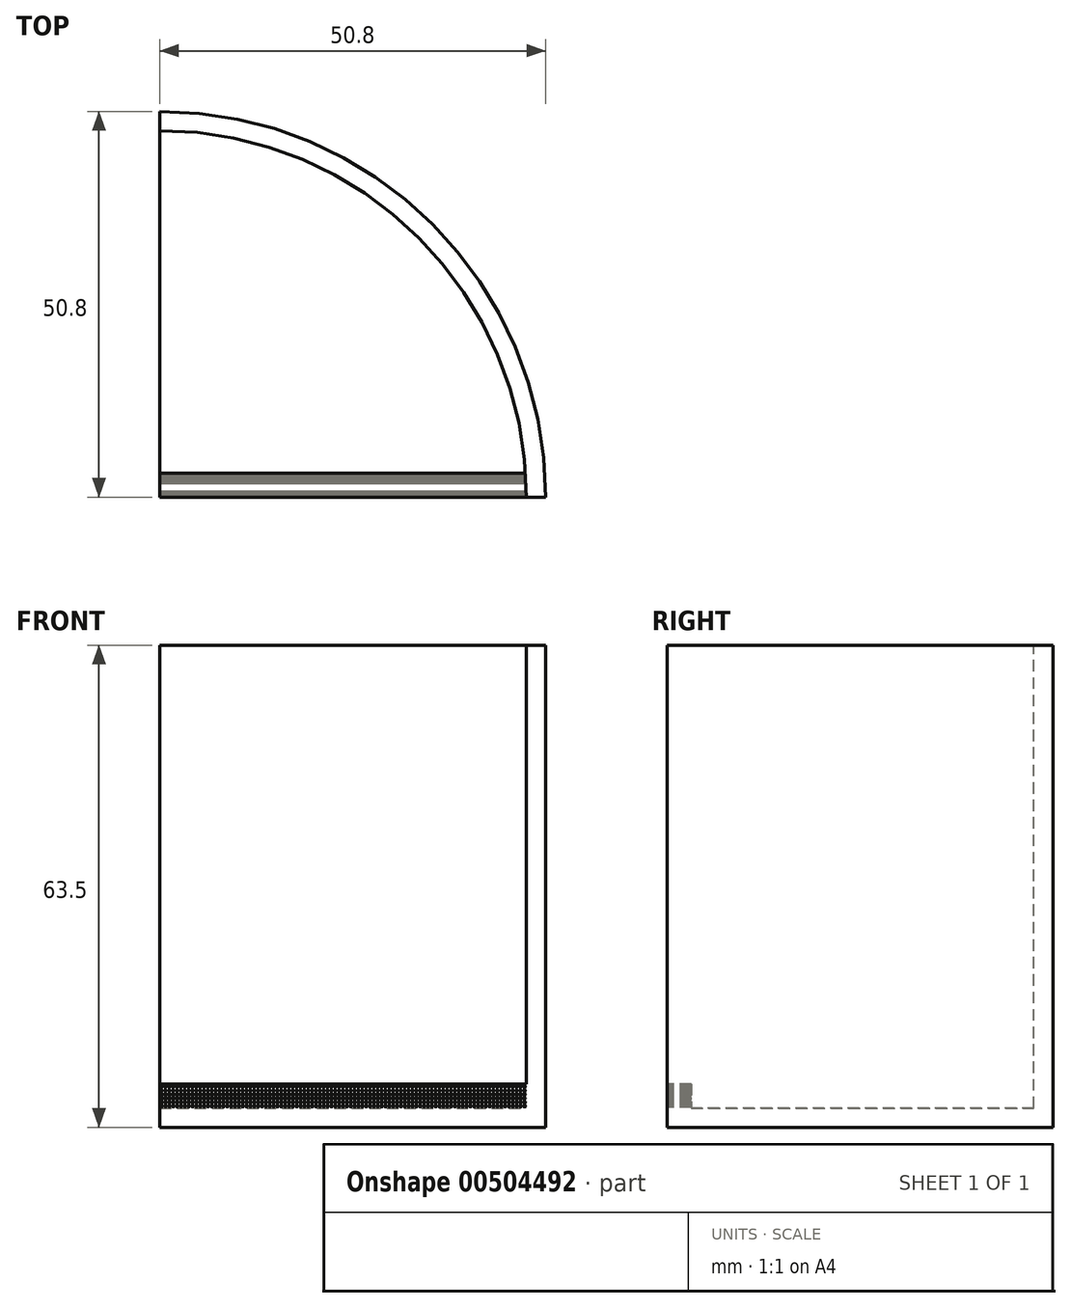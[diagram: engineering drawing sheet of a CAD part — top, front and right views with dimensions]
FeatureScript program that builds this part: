
annotation { "Feature Type Name" : "Feature", "Feature Type Description" : "" }
export const myFeature = defineFeature(function(context is Context, id is Id, definition is map)
    precondition{}
    {
        {
            var Q0;
            Q0=qCreatedBy(makeId("Front.planeOp"),FACE);
            var sketch = newSketch(context, id + "F0", { "sketchPlane" : qUnion([Q0])});
            skLineSegment(sketch, "E0", {"start": v(0, -22.85) * mm, "end": v(50.8, -22.85) * mm});
            skLineSegment(sketch, "E1", {"start": v(50.8, -22.85) * mm, "end": v(50.8, 40.65) * mm});
            skLineSegment(sketch, "E2", {"start": v(50.8, 40.65) * mm, "end": v(50.8, 40.65) * mm});
            skLineSegment(sketch, "E3", {"start": v(0, -22.85) * mm, "end": v(0, -20.3) * mm});
            skLineSegment(sketch, "E4", {"start": v(0, -20.3) * mm, "end": v(48.26, -20.3) * mm});
            skLineSegment(sketch, "E5", {"start": v(48.26, -20.3) * mm, "end": v(48.26, 40.65) * mm});
            skLineSegment(sketch, "E6", {"start": v(48.26, 40.65) * mm, "end": v(50.8, 40.65) * mm});
            skSolve(sketch);
        }
        {
            var Q0;
            Q0=makeQuery(id+"F0.imprint","IMPRINT",FACE,{"disambiguationData":[TD([[makeQuery(id+"F0.imprint","IMPRINT",EDGE,{"derivedFrom":sQuery(id+"F0.wireOp",EDGE,"E0")}),1.0]])]});
            var Q1;
            Q1=sQuery(id+"F0.wireOp",EDGE,"E3");
            revolve(context, id + "F1", {"entities" : qUnion([Q0]), "axis" : qUnion([Q1]), "revolveType" : RevolveType.ONE_DIRECTION, "angle" : 90 * degree});
        }
        {
            var Q0;
            Q0=makeQuery(id+"F1.opRevolve","CAP_FACE",FACE,{"disambiguationData":[OSD([sQuery(id+"F0.wireOp",EDGE,"E0"),sQuery(id+"F0.wireOp",EDGE,"E1"),sQuery(id+"F0.wireOp",EDGE,"E3"),sQuery(id+"F0.wireOp",EDGE,"E4"),sQuery(id+"F0.wireOp",EDGE,"E5"),sQuery(id+"F0.wireOp",EDGE,"E6")])],"isStart":true});
            var sketch = newSketch(context, id + "F2", { "sketchPlane" : qUnion([Q0])});
            skLineSegment(sketch, "E7.bottom", {"start": v(0, -20.3) * mm, "end": v(48.26, -20.3) * mm});
            skLineSegment(sketch, "E7.top", {"start": v(0, -17.13) * mm, "end": v(48.26, -17.13) * mm});
            skLineSegment(sketch, "E7.left", {"start": v(0, -20.3) * mm, "end": v(0, -17.13) * mm});
            skLineSegment(sketch, "E7.right", {"start": v(48.26, -20.3) * mm, "end": v(48.26, -17.13) * mm});
            skCircle(sketch, "E8", {"center": v(0.25, -20.05) * mm, "radius": 0.13 * mm});
            skLineSegment(sketch, "E9", {"start": v(0.25, -20.05) * mm, "end": v(0, -20.05) * mm});
            skCircle(sketch, "E10", {"center": v(0.25, -19.54) * mm, "radius": 0.13 * mm});
            skCircle(sketch, "E11", {"center": v(0.24, -19.04) * mm, "radius": 0.13 * mm});
            skCircle(sketch, "E12", {"center": v(0.24, -18.53) * mm, "radius": 0.13 * mm});
            skCircle(sketch, "E13", {"center": v(0.23, -18.02) * mm, "radius": 0.13 * mm});
            skCircle(sketch, "E14", {"center": v(0.23, -17.51) * mm, "radius": 0.13 * mm});
            skCircle(sketch, "E15.1.0.0", {"center": v(0.76, -20.05) * mm, "radius": 0.13 * mm});
            skCircle(sketch, "E15.2.0.0", {"center": v(1.27, -20.05) * mm, "radius": 0.13 * mm});
            skCircle(sketch, "E15.3.0.0", {"center": v(1.78, -20.05) * mm, "radius": 0.13 * mm});
            skCircle(sketch, "E15.4.0.0", {"center": v(2.29, -20.05) * mm, "radius": 0.13 * mm});
            skCircle(sketch, "E15.5.0.0", {"center": v(2.8, -20.05) * mm, "radius": 0.13 * mm});
            skCircle(sketch, "E15.6.0.0", {"center": v(3.3, -20.05) * mm, "radius": 0.13 * mm});
            skCircle(sketch, "E15.7.0.0", {"center": v(3.81, -20.05) * mm, "radius": 0.13 * mm});
            skCircle(sketch, "E15.8.0.0", {"center": v(4.32, -20.05) * mm, "radius": 0.13 * mm});
            skCircle(sketch, "E15.9.0.0", {"center": v(4.83, -20.05) * mm, "radius": 0.13 * mm});
            skCircle(sketch, "E15.10.0.0", {"center": v(5.33, -20.05) * mm, "radius": 0.13 * mm});
            skCircle(sketch, "E15.11.0.0", {"center": v(5.84, -20.05) * mm, "radius": 0.13 * mm});
            skCircle(sketch, "E15.12.0.0", {"center": v(6.35, -20.05) * mm, "radius": 0.13 * mm});
            skCircle(sketch, "E15.13.0.0", {"center": v(6.86, -20.05) * mm, "radius": 0.13 * mm});
            skCircle(sketch, "E15.14.0.0", {"center": v(7.37, -20.05) * mm, "radius": 0.13 * mm});
            skCircle(sketch, "E15.15.0.0", {"center": v(7.87, -20.05) * mm, "radius": 0.13 * mm});
            skCircle(sketch, "E15.16.0.0", {"center": v(8.38, -20.05) * mm, "radius": 0.13 * mm});
            skCircle(sketch, "E15.17.0.0", {"center": v(8.9, -20.05) * mm, "radius": 0.13 * mm});
            skCircle(sketch, "E15.18.0.0", {"center": v(9.4, -20.05) * mm, "radius": 0.13 * mm});
            skCircle(sketch, "E15.19.0.0", {"center": v(9.9, -20.05) * mm, "radius": 0.13 * mm});
            skCircle(sketch, "E15.20.0.0", {"center": v(10.41, -20.05) * mm, "radius": 0.13 * mm});
            skCircle(sketch, "E15.21.0.0", {"center": v(10.92, -20.05) * mm, "radius": 0.13 * mm});
            skCircle(sketch, "E15.22.0.0", {"center": v(11.43, -20.05) * mm, "radius": 0.13 * mm});
            skCircle(sketch, "E15.23.0.0", {"center": v(11.94, -20.05) * mm, "radius": 0.13 * mm});
            skCircle(sketch, "E15.24.0.0", {"center": v(12.45, -20.05) * mm, "radius": 0.13 * mm});
            skCircle(sketch, "E15.25.0.0", {"center": v(12.95, -20.05) * mm, "radius": 0.13 * mm});
            skCircle(sketch, "E15.26.0.0", {"center": v(13.46, -20.05) * mm, "radius": 0.13 * mm});
            skCircle(sketch, "E15.27.0.0", {"center": v(13.97, -20.05) * mm, "radius": 0.13 * mm});
            skCircle(sketch, "E15.28.0.0", {"center": v(14.48, -20.05) * mm, "radius": 0.13 * mm});
            skCircle(sketch, "E15.29.0.0", {"center": v(14.99, -20.05) * mm, "radius": 0.13 * mm});
            skCircle(sketch, "E15.30.0.0", {"center": v(15.5, -20.05) * mm, "radius": 0.13 * mm});
            skCircle(sketch, "E15.31.0.0", {"center": v(16, -20.05) * mm, "radius": 0.13 * mm});
            skCircle(sketch, "E15.32.0.0", {"center": v(16.51, -20.05) * mm, "radius": 0.13 * mm});
            skCircle(sketch, "E15.33.0.0", {"center": v(17.02, -20.05) * mm, "radius": 0.13 * mm});
            skCircle(sketch, "E15.34.0.0", {"center": v(17.53, -20.05) * mm, "radius": 0.13 * mm});
            skCircle(sketch, "E15.35.0.0", {"center": v(18.03, -20.05) * mm, "radius": 0.13 * mm});
            skCircle(sketch, "E15.36.0.0", {"center": v(18.54, -20.05) * mm, "radius": 0.13 * mm});
            skCircle(sketch, "E15.37.0.0", {"center": v(19.05, -20.05) * mm, "radius": 0.13 * mm});
            skCircle(sketch, "E15.38.0.0", {"center": v(19.56, -20.05) * mm, "radius": 0.13 * mm});
            skCircle(sketch, "E15.39.0.0", {"center": v(20.07, -20.05) * mm, "radius": 0.13 * mm});
            skCircle(sketch, "E15.40.0.0", {"center": v(20.57, -20.05) * mm, "radius": 0.13 * mm});
            skCircle(sketch, "E15.41.0.0", {"center": v(21.08, -20.05) * mm, "radius": 0.13 * mm});
            skCircle(sketch, "E15.42.0.0", {"center": v(21.6, -20.05) * mm, "radius": 0.13 * mm});
            skCircle(sketch, "E15.43.0.0", {"center": v(22.1, -20.05) * mm, "radius": 0.13 * mm});
            skCircle(sketch, "E15.44.0.0", {"center": v(22.6, -20.05) * mm, "radius": 0.13 * mm});
            skCircle(sketch, "E15.45.0.0", {"center": v(23.11, -20.05) * mm, "radius": 0.13 * mm});
            skCircle(sketch, "E15.46.0.0", {"center": v(23.62, -20.05) * mm, "radius": 0.13 * mm});
            skCircle(sketch, "E15.47.0.0", {"center": v(24.13, -20.05) * mm, "radius": 0.13 * mm});
            skCircle(sketch, "E15.48.0.0", {"center": v(24.64, -20.05) * mm, "radius": 0.13 * mm});
            skCircle(sketch, "E15.49.0.0", {"center": v(25.15, -20.05) * mm, "radius": 0.13 * mm});
            skCircle(sketch, "E15.50.0.0", {"center": v(25.65, -20.05) * mm, "radius": 0.13 * mm});
            skCircle(sketch, "E15.51.0.0", {"center": v(26.16, -20.05) * mm, "radius": 0.13 * mm});
            skCircle(sketch, "E15.52.0.0", {"center": v(26.67, -20.05) * mm, "radius": 0.13 * mm});
            skCircle(sketch, "E15.53.0.0", {"center": v(27.18, -20.05) * mm, "radius": 0.13 * mm});
            skCircle(sketch, "E15.54.0.0", {"center": v(27.69, -20.05) * mm, "radius": 0.13 * mm});
            skCircle(sketch, "E15.55.0.0", {"center": v(28.2, -20.05) * mm, "radius": 0.13 * mm});
            skCircle(sketch, "E15.56.0.0", {"center": v(28.7, -20.05) * mm, "radius": 0.13 * mm});
            skCircle(sketch, "E15.57.0.0", {"center": v(29.21, -20.05) * mm, "radius": 0.13 * mm});
            skCircle(sketch, "E15.58.0.0", {"center": v(29.72, -20.05) * mm, "radius": 0.13 * mm});
            skCircle(sketch, "E15.59.0.0", {"center": v(30.23, -20.05) * mm, "radius": 0.13 * mm});
            skCircle(sketch, "E15.60.0.0", {"center": v(30.73, -20.05) * mm, "radius": 0.13 * mm});
            skCircle(sketch, "E15.61.0.0", {"center": v(31.24, -20.05) * mm, "radius": 0.13 * mm});
            skCircle(sketch, "E15.62.0.0", {"center": v(31.75, -20.05) * mm, "radius": 0.13 * mm});
            skCircle(sketch, "E15.63.0.0", {"center": v(32.26, -20.05) * mm, "radius": 0.13 * mm});
            skCircle(sketch, "E15.64.0.0", {"center": v(32.77, -20.05) * mm, "radius": 0.13 * mm});
            skCircle(sketch, "E15.65.0.0", {"center": v(33.27, -20.05) * mm, "radius": 0.13 * mm});
            skCircle(sketch, "E15.66.0.0", {"center": v(33.78, -20.05) * mm, "radius": 0.13 * mm});
            skCircle(sketch, "E15.67.0.0", {"center": v(34.3, -20.05) * mm, "radius": 0.13 * mm});
            skCircle(sketch, "E15.68.0.0", {"center": v(34.8, -20.05) * mm, "radius": 0.13 * mm});
            skCircle(sketch, "E15.69.0.0", {"center": v(35.3, -20.05) * mm, "radius": 0.13 * mm});
            skCircle(sketch, "E15.70.0.0", {"center": v(35.81, -20.05) * mm, "radius": 0.13 * mm});
            skCircle(sketch, "E15.71.0.0", {"center": v(36.32, -20.05) * mm, "radius": 0.13 * mm});
            skCircle(sketch, "E15.72.0.0", {"center": v(36.83, -20.05) * mm, "radius": 0.13 * mm});
            skCircle(sketch, "E15.73.0.0", {"center": v(37.34, -20.05) * mm, "radius": 0.13 * mm});
            skCircle(sketch, "E15.74.0.0", {"center": v(37.85, -20.05) * mm, "radius": 0.13 * mm});
            skCircle(sketch, "E15.75.0.0", {"center": v(38.35, -20.05) * mm, "radius": 0.13 * mm});
            skCircle(sketch, "E15.76.0.0", {"center": v(38.86, -20.05) * mm, "radius": 0.13 * mm});
            skCircle(sketch, "E15.77.0.0", {"center": v(39.37, -20.05) * mm, "radius": 0.13 * mm});
            skCircle(sketch, "E15.78.0.0", {"center": v(39.88, -20.05) * mm, "radius": 0.13 * mm});
            skCircle(sketch, "E15.79.0.0", {"center": v(40.39, -20.05) * mm, "radius": 0.13 * mm});
            skCircle(sketch, "E15.80.0.0", {"center": v(40.9, -20.05) * mm, "radius": 0.13 * mm});
            skCircle(sketch, "E15.81.0.0", {"center": v(41.4, -20.05) * mm, "radius": 0.13 * mm});
            skCircle(sketch, "E15.82.0.0", {"center": v(41.91, -20.05) * mm, "radius": 0.13 * mm});
            skCircle(sketch, "E15.83.0.0", {"center": v(42.42, -20.05) * mm, "radius": 0.13 * mm});
            skCircle(sketch, "E15.84.0.0", {"center": v(42.93, -20.05) * mm, "radius": 0.13 * mm});
            skCircle(sketch, "E15.85.0.0", {"center": v(43.43, -20.05) * mm, "radius": 0.13 * mm});
            skCircle(sketch, "E15.86.0.0", {"center": v(43.94, -20.05) * mm, "radius": 0.13 * mm});
            skCircle(sketch, "E15.87.0.0", {"center": v(44.45, -20.05) * mm, "radius": 0.13 * mm});
            skCircle(sketch, "E15.88.0.0", {"center": v(44.96, -20.05) * mm, "radius": 0.13 * mm});
            skCircle(sketch, "E15.89.0.0", {"center": v(45.47, -20.05) * mm, "radius": 0.13 * mm});
            skCircle(sketch, "E15.90.0.0", {"center": v(45.97, -20.05) * mm, "radius": 0.13 * mm});
            skCircle(sketch, "E15.91.0.0", {"center": v(46.48, -20.05) * mm, "radius": 0.13 * mm});
            skCircle(sketch, "E15.92.0.0", {"center": v(47, -20.05) * mm, "radius": 0.13 * mm});
            skCircle(sketch, "E15.93.0.0", {"center": v(47.5, -20.05) * mm, "radius": 0.13 * mm});
            skCircle(sketch, "E15.94.0.0", {"center": v(48, -20.05) * mm, "radius": 0.13 * mm});
            skLineSegment(sketch, "E15.direction1", {"start": v(0.25, -20.05) * mm, "end": v(0.76, -20.05) * mm, "construction": true});
            skCircle(sketch, "E16.1.0.0", {"center": v(0.76, -19.54) * mm, "radius": 0.13 * mm});
            skCircle(sketch, "E16.2.0.0", {"center": v(1.26, -19.54) * mm, "radius": 0.13 * mm});
            skCircle(sketch, "E16.3.0.0", {"center": v(1.77, -19.54) * mm, "radius": 0.13 * mm});
            skCircle(sketch, "E16.4.0.0", {"center": v(2.28, -19.54) * mm, "radius": 0.13 * mm});
            skCircle(sketch, "E16.5.0.0", {"center": v(2.79, -19.54) * mm, "radius": 0.13 * mm});
            skCircle(sketch, "E16.6.0.0", {"center": v(3.3, -19.54) * mm, "radius": 0.13 * mm});
            skCircle(sketch, "E16.7.0.0", {"center": v(3.8, -19.54) * mm, "radius": 0.13 * mm});
            skCircle(sketch, "E16.8.0.0", {"center": v(4.31, -19.54) * mm, "radius": 0.13 * mm});
            skCircle(sketch, "E16.9.0.0", {"center": v(4.82, -19.54) * mm, "radius": 0.13 * mm});
            skCircle(sketch, "E16.10.0.0", {"center": v(5.33, -19.54) * mm, "radius": 0.13 * mm});
            skCircle(sketch, "E16.11.0.0", {"center": v(5.84, -19.54) * mm, "radius": 0.13 * mm});
            skCircle(sketch, "E16.12.0.0", {"center": v(6.34, -19.54) * mm, "radius": 0.13 * mm});
            skCircle(sketch, "E16.13.0.0", {"center": v(6.85, -19.54) * mm, "radius": 0.13 * mm});
            skCircle(sketch, "E16.14.0.0", {"center": v(7.36, -19.54) * mm, "radius": 0.13 * mm});
            skCircle(sketch, "E16.15.0.0", {"center": v(7.87, -19.54) * mm, "radius": 0.13 * mm});
            skCircle(sketch, "E16.16.0.0", {"center": v(8.38, -19.54) * mm, "radius": 0.13 * mm});
            skCircle(sketch, "E16.17.0.0", {"center": v(8.88, -19.54) * mm, "radius": 0.13 * mm});
            skCircle(sketch, "E16.18.0.0", {"center": v(9.4, -19.54) * mm, "radius": 0.13 * mm});
            skCircle(sketch, "E16.19.0.0", {"center": v(9.9, -19.54) * mm, "radius": 0.13 * mm});
            skCircle(sketch, "E16.20.0.0", {"center": v(10.4, -19.54) * mm, "radius": 0.13 * mm});
            skCircle(sketch, "E16.21.0.0", {"center": v(10.92, -19.54) * mm, "radius": 0.13 * mm});
            skCircle(sketch, "E16.22.0.0", {"center": v(11.42, -19.54) * mm, "radius": 0.13 * mm});
            skCircle(sketch, "E16.23.0.0", {"center": v(11.93, -19.54) * mm, "radius": 0.13 * mm});
            skCircle(sketch, "E16.24.0.0", {"center": v(12.44, -19.54) * mm, "radius": 0.13 * mm});
            skCircle(sketch, "E16.25.0.0", {"center": v(12.95, -19.54) * mm, "radius": 0.13 * mm});
            skCircle(sketch, "E16.26.0.0", {"center": v(13.46, -19.54) * mm, "radius": 0.13 * mm});
            skCircle(sketch, "E16.27.0.0", {"center": v(13.96, -19.54) * mm, "radius": 0.13 * mm});
            skCircle(sketch, "E16.28.0.0", {"center": v(14.47, -19.54) * mm, "radius": 0.13 * mm});
            skCircle(sketch, "E16.29.0.0", {"center": v(14.98, -19.54) * mm, "radius": 0.13 * mm});
            skCircle(sketch, "E16.30.0.0", {"center": v(15.49, -19.54) * mm, "radius": 0.13 * mm});
            skCircle(sketch, "E16.31.0.0", {"center": v(16, -19.54) * mm, "radius": 0.13 * mm});
            skCircle(sketch, "E16.32.0.0", {"center": v(16.5, -19.54) * mm, "radius": 0.13 * mm});
            skCircle(sketch, "E16.33.0.0", {"center": v(17.01, -19.54) * mm, "radius": 0.13 * mm});
            skCircle(sketch, "E16.34.0.0", {"center": v(17.52, -19.54) * mm, "radius": 0.13 * mm});
            skCircle(sketch, "E16.35.0.0", {"center": v(18.03, -19.54) * mm, "radius": 0.13 * mm});
            skCircle(sketch, "E16.36.0.0", {"center": v(18.54, -19.54) * mm, "radius": 0.13 * mm});
            skCircle(sketch, "E16.37.0.0", {"center": v(19.04, -19.54) * mm, "radius": 0.13 * mm});
            skCircle(sketch, "E16.38.0.0", {"center": v(19.55, -19.54) * mm, "radius": 0.13 * mm});
            skCircle(sketch, "E16.39.0.0", {"center": v(20.06, -19.54) * mm, "radius": 0.13 * mm});
            skCircle(sketch, "E16.40.0.0", {"center": v(20.57, -19.54) * mm, "radius": 0.13 * mm});
            skCircle(sketch, "E16.41.0.0", {"center": v(21.08, -19.54) * mm, "radius": 0.13 * mm});
            skCircle(sketch, "E16.42.0.0", {"center": v(21.58, -19.54) * mm, "radius": 0.13 * mm});
            skCircle(sketch, "E16.43.0.0", {"center": v(22.1, -19.54) * mm, "radius": 0.13 * mm});
            skCircle(sketch, "E16.44.0.0", {"center": v(22.6, -19.54) * mm, "radius": 0.13 * mm});
            skCircle(sketch, "E16.45.0.0", {"center": v(23.1, -19.54) * mm, "radius": 0.13 * mm});
            skCircle(sketch, "E16.46.0.0", {"center": v(23.62, -19.54) * mm, "radius": 0.13 * mm});
            skCircle(sketch, "E16.47.0.0", {"center": v(24.12, -19.54) * mm, "radius": 0.13 * mm});
            skCircle(sketch, "E16.48.0.0", {"center": v(24.63, -19.54) * mm, "radius": 0.13 * mm});
            skCircle(sketch, "E16.49.0.0", {"center": v(25.14, -19.54) * mm, "radius": 0.13 * mm});
            skCircle(sketch, "E16.50.0.0", {"center": v(25.65, -19.54) * mm, "radius": 0.13 * mm});
            skCircle(sketch, "E16.51.0.0", {"center": v(26.16, -19.54) * mm, "radius": 0.13 * mm});
            skCircle(sketch, "E16.52.0.0", {"center": v(26.66, -19.54) * mm, "radius": 0.13 * mm});
            skCircle(sketch, "E16.53.0.0", {"center": v(27.17, -19.54) * mm, "radius": 0.13 * mm});
            skCircle(sketch, "E16.54.0.0", {"center": v(27.68, -19.54) * mm, "radius": 0.13 * mm});
            skCircle(sketch, "E16.55.0.0", {"center": v(28.19, -19.54) * mm, "radius": 0.13 * mm});
            skCircle(sketch, "E16.56.0.0", {"center": v(28.7, -19.54) * mm, "radius": 0.13 * mm});
            skCircle(sketch, "E16.57.0.0", {"center": v(29.2, -19.54) * mm, "radius": 0.13 * mm});
            skCircle(sketch, "E16.58.0.0", {"center": v(29.71, -19.54) * mm, "radius": 0.13 * mm});
            skCircle(sketch, "E16.59.0.0", {"center": v(30.22, -19.54) * mm, "radius": 0.13 * mm});
            skCircle(sketch, "E16.60.0.0", {"center": v(30.73, -19.54) * mm, "radius": 0.13 * mm});
            skCircle(sketch, "E16.61.0.0", {"center": v(31.24, -19.54) * mm, "radius": 0.13 * mm});
            skCircle(sketch, "E16.62.0.0", {"center": v(31.74, -19.54) * mm, "radius": 0.13 * mm});
            skCircle(sketch, "E16.63.0.0", {"center": v(32.25, -19.54) * mm, "radius": 0.13 * mm});
            skCircle(sketch, "E16.64.0.0", {"center": v(32.76, -19.54) * mm, "radius": 0.13 * mm});
            skCircle(sketch, "E16.65.0.0", {"center": v(33.27, -19.54) * mm, "radius": 0.13 * mm});
            skCircle(sketch, "E16.66.0.0", {"center": v(33.78, -19.54) * mm, "radius": 0.13 * mm});
            skCircle(sketch, "E16.67.0.0", {"center": v(34.28, -19.54) * mm, "radius": 0.13 * mm});
            skCircle(sketch, "E16.68.0.0", {"center": v(34.8, -19.54) * mm, "radius": 0.13 * mm});
            skCircle(sketch, "E16.69.0.0", {"center": v(35.3, -19.54) * mm, "radius": 0.13 * mm});
            skCircle(sketch, "E16.70.0.0", {"center": v(35.8, -19.54) * mm, "radius": 0.13 * mm});
            skCircle(sketch, "E16.71.0.0", {"center": v(36.32, -19.54) * mm, "radius": 0.13 * mm});
            skCircle(sketch, "E16.72.0.0", {"center": v(36.82, -19.54) * mm, "radius": 0.13 * mm});
            skCircle(sketch, "E16.73.0.0", {"center": v(37.33, -19.54) * mm, "radius": 0.13 * mm});
            skCircle(sketch, "E16.74.0.0", {"center": v(37.84, -19.54) * mm, "radius": 0.13 * mm});
            skCircle(sketch, "E16.75.0.0", {"center": v(38.35, -19.54) * mm, "radius": 0.13 * mm});
            skCircle(sketch, "E16.76.0.0", {"center": v(38.86, -19.54) * mm, "radius": 0.13 * mm});
            skCircle(sketch, "E16.77.0.0", {"center": v(39.36, -19.54) * mm, "radius": 0.13 * mm});
            skCircle(sketch, "E16.78.0.0", {"center": v(39.87, -19.54) * mm, "radius": 0.13 * mm});
            skCircle(sketch, "E16.79.0.0", {"center": v(40.38, -19.54) * mm, "radius": 0.13 * mm});
            skCircle(sketch, "E16.80.0.0", {"center": v(40.89, -19.54) * mm, "radius": 0.13 * mm});
            skCircle(sketch, "E16.81.0.0", {"center": v(41.4, -19.54) * mm, "radius": 0.13 * mm});
            skCircle(sketch, "E16.82.0.0", {"center": v(41.9, -19.54) * mm, "radius": 0.13 * mm});
            skCircle(sketch, "E16.83.0.0", {"center": v(42.41, -19.54) * mm, "radius": 0.13 * mm});
            skCircle(sketch, "E16.84.0.0", {"center": v(42.92, -19.54) * mm, "radius": 0.13 * mm});
            skCircle(sketch, "E16.85.0.0", {"center": v(43.43, -19.54) * mm, "radius": 0.13 * mm});
            skCircle(sketch, "E16.86.0.0", {"center": v(43.94, -19.54) * mm, "radius": 0.13 * mm});
            skCircle(sketch, "E16.87.0.0", {"center": v(44.44, -19.54) * mm, "radius": 0.13 * mm});
            skCircle(sketch, "E16.88.0.0", {"center": v(44.95, -19.54) * mm, "radius": 0.13 * mm});
            skCircle(sketch, "E16.89.0.0", {"center": v(45.46, -19.54) * mm, "radius": 0.13 * mm});
            skCircle(sketch, "E16.90.0.0", {"center": v(45.97, -19.54) * mm, "radius": 0.13 * mm});
            skCircle(sketch, "E16.91.0.0", {"center": v(46.48, -19.54) * mm, "radius": 0.13 * mm});
            skCircle(sketch, "E16.92.0.0", {"center": v(46.98, -19.54) * mm, "radius": 0.13 * mm});
            skCircle(sketch, "E16.93.0.0", {"center": v(47.5, -19.54) * mm, "radius": 0.13 * mm});
            skCircle(sketch, "E16.94.0.0", {"center": v(48, -19.54) * mm, "radius": 0.13 * mm});
            skLineSegment(sketch, "E16.direction1", {"start": v(0.25, -19.54) * mm, "end": v(0.76, -19.54) * mm, "construction": true});
            skCircle(sketch, "E17.1.0.0", {"center": v(0.75, -19.04) * mm, "radius": 0.13 * mm});
            skCircle(sketch, "E17.2.0.0", {"center": v(1.26, -19.04) * mm, "radius": 0.13 * mm});
            skCircle(sketch, "E17.3.0.0", {"center": v(1.77, -19.04) * mm, "radius": 0.13 * mm});
            skCircle(sketch, "E17.4.0.0", {"center": v(2.28, -19.04) * mm, "radius": 0.13 * mm});
            skCircle(sketch, "E17.5.0.0", {"center": v(2.78, -19.04) * mm, "radius": 0.13 * mm});
            skCircle(sketch, "E17.6.0.0", {"center": v(3.3, -19.04) * mm, "radius": 0.13 * mm});
            skCircle(sketch, "E17.7.0.0", {"center": v(3.8, -19.04) * mm, "radius": 0.13 * mm});
            skCircle(sketch, "E17.8.0.0", {"center": v(4.3, -19.04) * mm, "radius": 0.13 * mm});
            skCircle(sketch, "E17.9.0.0", {"center": v(4.82, -19.04) * mm, "radius": 0.13 * mm});
            skCircle(sketch, "E17.10.0.0", {"center": v(5.32, -19.04) * mm, "radius": 0.13 * mm});
            skCircle(sketch, "E17.11.0.0", {"center": v(5.83, -19.04) * mm, "radius": 0.13 * mm});
            skCircle(sketch, "E17.12.0.0", {"center": v(6.34, -19.04) * mm, "radius": 0.13 * mm});
            skCircle(sketch, "E17.13.0.0", {"center": v(6.85, -19.04) * mm, "radius": 0.13 * mm});
            skCircle(sketch, "E17.14.0.0", {"center": v(7.36, -19.04) * mm, "radius": 0.13 * mm});
            skCircle(sketch, "E17.15.0.0", {"center": v(7.86, -19.04) * mm, "radius": 0.13 * mm});
            skCircle(sketch, "E17.16.0.0", {"center": v(8.37, -19.04) * mm, "radius": 0.13 * mm});
            skCircle(sketch, "E17.17.0.0", {"center": v(8.88, -19.04) * mm, "radius": 0.13 * mm});
            skCircle(sketch, "E17.18.0.0", {"center": v(9.39, -19.04) * mm, "radius": 0.13 * mm});
            skCircle(sketch, "E17.19.0.0", {"center": v(9.9, -19.04) * mm, "radius": 0.13 * mm});
            skCircle(sketch, "E17.20.0.0", {"center": v(10.4, -19.04) * mm, "radius": 0.13 * mm});
            skCircle(sketch, "E17.21.0.0", {"center": v(10.91, -19.04) * mm, "radius": 0.13 * mm});
            skCircle(sketch, "E17.22.0.0", {"center": v(11.42, -19.04) * mm, "radius": 0.13 * mm});
            skCircle(sketch, "E17.23.0.0", {"center": v(11.93, -19.04) * mm, "radius": 0.13 * mm});
            skCircle(sketch, "E17.24.0.0", {"center": v(12.44, -19.04) * mm, "radius": 0.13 * mm});
            skCircle(sketch, "E17.25.0.0", {"center": v(12.94, -19.04) * mm, "radius": 0.13 * mm});
            skCircle(sketch, "E17.26.0.0", {"center": v(13.45, -19.04) * mm, "radius": 0.13 * mm});
            skCircle(sketch, "E17.27.0.0", {"center": v(13.96, -19.04) * mm, "radius": 0.13 * mm});
            skCircle(sketch, "E17.28.0.0", {"center": v(14.47, -19.04) * mm, "radius": 0.13 * mm});
            skCircle(sketch, "E17.29.0.0", {"center": v(14.98, -19.04) * mm, "radius": 0.13 * mm});
            skCircle(sketch, "E17.30.0.0", {"center": v(15.48, -19.04) * mm, "radius": 0.13 * mm});
            skCircle(sketch, "E17.31.0.0", {"center": v(16, -19.04) * mm, "radius": 0.13 * mm});
            skCircle(sketch, "E17.32.0.0", {"center": v(16.5, -19.04) * mm, "radius": 0.13 * mm});
            skCircle(sketch, "E17.33.0.0", {"center": v(17, -19.04) * mm, "radius": 0.13 * mm});
            skCircle(sketch, "E17.34.0.0", {"center": v(17.52, -19.04) * mm, "radius": 0.13 * mm});
            skCircle(sketch, "E17.35.0.0", {"center": v(18.02, -19.04) * mm, "radius": 0.13 * mm});
            skCircle(sketch, "E17.36.0.0", {"center": v(18.53, -19.04) * mm, "radius": 0.13 * mm});
            skCircle(sketch, "E17.37.0.0", {"center": v(19.04, -19.04) * mm, "radius": 0.13 * mm});
            skCircle(sketch, "E17.38.0.0", {"center": v(19.55, -19.04) * mm, "radius": 0.13 * mm});
            skCircle(sketch, "E17.39.0.0", {"center": v(20.06, -19.04) * mm, "radius": 0.13 * mm});
            skCircle(sketch, "E17.40.0.0", {"center": v(20.56, -19.04) * mm, "radius": 0.13 * mm});
            skCircle(sketch, "E17.41.0.0", {"center": v(21.07, -19.04) * mm, "radius": 0.13 * mm});
            skCircle(sketch, "E17.42.0.0", {"center": v(21.58, -19.04) * mm, "radius": 0.13 * mm});
            skCircle(sketch, "E17.43.0.0", {"center": v(22.09, -19.04) * mm, "radius": 0.13 * mm});
            skCircle(sketch, "E17.44.0.0", {"center": v(22.6, -19.04) * mm, "radius": 0.13 * mm});
            skCircle(sketch, "E17.45.0.0", {"center": v(23.1, -19.04) * mm, "radius": 0.13 * mm});
            skCircle(sketch, "E17.46.0.0", {"center": v(23.61, -19.04) * mm, "radius": 0.13 * mm});
            skCircle(sketch, "E17.47.0.0", {"center": v(24.12, -19.04) * mm, "radius": 0.13 * mm});
            skCircle(sketch, "E17.48.0.0", {"center": v(24.63, -19.04) * mm, "radius": 0.13 * mm});
            skCircle(sketch, "E17.49.0.0", {"center": v(25.14, -19.04) * mm, "radius": 0.13 * mm});
            skCircle(sketch, "E17.50.0.0", {"center": v(25.64, -19.04) * mm, "radius": 0.13 * mm});
            skCircle(sketch, "E17.51.0.0", {"center": v(26.15, -19.04) * mm, "radius": 0.13 * mm});
            skCircle(sketch, "E17.52.0.0", {"center": v(26.66, -19.04) * mm, "radius": 0.13 * mm});
            skCircle(sketch, "E17.53.0.0", {"center": v(27.17, -19.04) * mm, "radius": 0.13 * mm});
            skCircle(sketch, "E17.54.0.0", {"center": v(27.68, -19.04) * mm, "radius": 0.13 * mm});
            skCircle(sketch, "E17.55.0.0", {"center": v(28.18, -19.04) * mm, "radius": 0.13 * mm});
            skCircle(sketch, "E17.56.0.0", {"center": v(28.7, -19.04) * mm, "radius": 0.13 * mm});
            skCircle(sketch, "E17.57.0.0", {"center": v(29.2, -19.04) * mm, "radius": 0.13 * mm});
            skCircle(sketch, "E17.58.0.0", {"center": v(29.7, -19.04) * mm, "radius": 0.13 * mm});
            skCircle(sketch, "E17.59.0.0", {"center": v(30.22, -19.04) * mm, "radius": 0.13 * mm});
            skCircle(sketch, "E17.60.0.0", {"center": v(30.72, -19.04) * mm, "radius": 0.13 * mm});
            skCircle(sketch, "E17.61.0.0", {"center": v(31.23, -19.04) * mm, "radius": 0.13 * mm});
            skCircle(sketch, "E17.62.0.0", {"center": v(31.74, -19.04) * mm, "radius": 0.13 * mm});
            skCircle(sketch, "E17.63.0.0", {"center": v(32.25, -19.04) * mm, "radius": 0.13 * mm});
            skCircle(sketch, "E17.64.0.0", {"center": v(32.76, -19.04) * mm, "radius": 0.13 * mm});
            skCircle(sketch, "E17.65.0.0", {"center": v(33.26, -19.04) * mm, "radius": 0.13 * mm});
            skCircle(sketch, "E17.66.0.0", {"center": v(33.77, -19.04) * mm, "radius": 0.13 * mm});
            skCircle(sketch, "E17.67.0.0", {"center": v(34.28, -19.04) * mm, "radius": 0.13 * mm});
            skCircle(sketch, "E17.68.0.0", {"center": v(34.79, -19.04) * mm, "radius": 0.13 * mm});
            skCircle(sketch, "E17.69.0.0", {"center": v(35.3, -19.04) * mm, "radius": 0.13 * mm});
            skCircle(sketch, "E17.70.0.0", {"center": v(35.8, -19.04) * mm, "radius": 0.13 * mm});
            skCircle(sketch, "E17.71.0.0", {"center": v(36.31, -19.04) * mm, "radius": 0.13 * mm});
            skCircle(sketch, "E17.72.0.0", {"center": v(36.82, -19.04) * mm, "radius": 0.13 * mm});
            skCircle(sketch, "E17.73.0.0", {"center": v(37.33, -19.04) * mm, "radius": 0.13 * mm});
            skCircle(sketch, "E17.74.0.0", {"center": v(37.84, -19.04) * mm, "radius": 0.13 * mm});
            skCircle(sketch, "E17.75.0.0", {"center": v(38.34, -19.04) * mm, "radius": 0.13 * mm});
            skCircle(sketch, "E17.76.0.0", {"center": v(38.85, -19.04) * mm, "radius": 0.13 * mm});
            skCircle(sketch, "E17.77.0.0", {"center": v(39.36, -19.04) * mm, "radius": 0.13 * mm});
            skCircle(sketch, "E17.78.0.0", {"center": v(39.87, -19.04) * mm, "radius": 0.13 * mm});
            skCircle(sketch, "E17.79.0.0", {"center": v(40.38, -19.04) * mm, "radius": 0.13 * mm});
            skCircle(sketch, "E17.80.0.0", {"center": v(40.88, -19.04) * mm, "radius": 0.13 * mm});
            skCircle(sketch, "E17.81.0.0", {"center": v(41.4, -19.04) * mm, "radius": 0.13 * mm});
            skCircle(sketch, "E17.82.0.0", {"center": v(41.9, -19.04) * mm, "radius": 0.13 * mm});
            skCircle(sketch, "E17.83.0.0", {"center": v(42.4, -19.04) * mm, "radius": 0.13 * mm});
            skCircle(sketch, "E17.84.0.0", {"center": v(42.92, -19.04) * mm, "radius": 0.13 * mm});
            skCircle(sketch, "E17.85.0.0", {"center": v(43.42, -19.04) * mm, "radius": 0.13 * mm});
            skCircle(sketch, "E17.86.0.0", {"center": v(43.93, -19.04) * mm, "radius": 0.13 * mm});
            skCircle(sketch, "E17.87.0.0", {"center": v(44.44, -19.04) * mm, "radius": 0.13 * mm});
            skCircle(sketch, "E17.88.0.0", {"center": v(44.95, -19.04) * mm, "radius": 0.13 * mm});
            skCircle(sketch, "E17.89.0.0", {"center": v(45.46, -19.04) * mm, "radius": 0.13 * mm});
            skCircle(sketch, "E17.90.0.0", {"center": v(45.96, -19.04) * mm, "radius": 0.13 * mm});
            skCircle(sketch, "E17.91.0.0", {"center": v(46.47, -19.04) * mm, "radius": 0.13 * mm});
            skCircle(sketch, "E17.92.0.0", {"center": v(46.98, -19.04) * mm, "radius": 0.13 * mm});
            skCircle(sketch, "E17.93.0.0", {"center": v(47.49, -19.04) * mm, "radius": 0.13 * mm});
            skCircle(sketch, "E17.94.0.0", {"center": v(48, -19.04) * mm, "radius": 0.13 * mm});
            skLineSegment(sketch, "E17.direction1", {"start": v(0.24, -19.04) * mm, "end": v(0.75, -19.04) * mm, "construction": true});
            skCircle(sketch, "E18.1.0.0", {"center": v(0.75, -18.53) * mm, "radius": 0.13 * mm});
            skCircle(sketch, "E18.2.0.0", {"center": v(1.25, -18.53) * mm, "radius": 0.13 * mm});
            skCircle(sketch, "E18.3.0.0", {"center": v(1.76, -18.53) * mm, "radius": 0.13 * mm});
            skCircle(sketch, "E18.4.0.0", {"center": v(2.27, -18.53) * mm, "radius": 0.13 * mm});
            skCircle(sketch, "E18.5.0.0", {"center": v(2.78, -18.53) * mm, "radius": 0.13 * mm});
            skCircle(sketch, "E18.6.0.0", {"center": v(3.29, -18.53) * mm, "radius": 0.13 * mm});
            skCircle(sketch, "E18.7.0.0", {"center": v(3.8, -18.53) * mm, "radius": 0.13 * mm});
            skCircle(sketch, "E18.8.0.0", {"center": v(4.3, -18.53) * mm, "radius": 0.13 * mm});
            skCircle(sketch, "E18.9.0.0", {"center": v(4.81, -18.53) * mm, "radius": 0.13 * mm});
            skCircle(sketch, "E18.10.0.0", {"center": v(5.32, -18.53) * mm, "radius": 0.13 * mm});
            skCircle(sketch, "E18.11.0.0", {"center": v(5.83, -18.53) * mm, "radius": 0.13 * mm});
            skCircle(sketch, "E18.12.0.0", {"center": v(6.33, -18.53) * mm, "radius": 0.13 * mm});
            skCircle(sketch, "E18.13.0.0", {"center": v(6.84, -18.53) * mm, "radius": 0.13 * mm});
            skCircle(sketch, "E18.14.0.0", {"center": v(7.35, -18.53) * mm, "radius": 0.13 * mm});
            skCircle(sketch, "E18.15.0.0", {"center": v(7.86, -18.53) * mm, "radius": 0.13 * mm});
            skCircle(sketch, "E18.16.0.0", {"center": v(8.37, -18.53) * mm, "radius": 0.13 * mm});
            skCircle(sketch, "E18.17.0.0", {"center": v(8.87, -18.53) * mm, "radius": 0.13 * mm});
            skCircle(sketch, "E18.18.0.0", {"center": v(9.38, -18.53) * mm, "radius": 0.13 * mm});
            skCircle(sketch, "E18.19.0.0", {"center": v(9.9, -18.53) * mm, "radius": 0.13 * mm});
            skCircle(sketch, "E18.20.0.0", {"center": v(10.4, -18.53) * mm, "radius": 0.13 * mm});
            skCircle(sketch, "E18.21.0.0", {"center": v(10.9, -18.53) * mm, "radius": 0.13 * mm});
            skCircle(sketch, "E18.22.0.0", {"center": v(11.41, -18.53) * mm, "radius": 0.13 * mm});
            skCircle(sketch, "E18.23.0.0", {"center": v(11.92, -18.53) * mm, "radius": 0.13 * mm});
            skCircle(sketch, "E18.24.0.0", {"center": v(12.43, -18.53) * mm, "radius": 0.13 * mm});
            skCircle(sketch, "E18.25.0.0", {"center": v(12.94, -18.53) * mm, "radius": 0.13 * mm});
            skCircle(sketch, "E18.26.0.0", {"center": v(13.45, -18.53) * mm, "radius": 0.13 * mm});
            skCircle(sketch, "E18.27.0.0", {"center": v(13.95, -18.53) * mm, "radius": 0.13 * mm});
            skCircle(sketch, "E18.28.0.0", {"center": v(14.46, -18.53) * mm, "radius": 0.13 * mm});
            skCircle(sketch, "E18.29.0.0", {"center": v(14.97, -18.53) * mm, "radius": 0.13 * mm});
            skCircle(sketch, "E18.30.0.0", {"center": v(15.48, -18.53) * mm, "radius": 0.13 * mm});
            skCircle(sketch, "E18.31.0.0", {"center": v(15.99, -18.53) * mm, "radius": 0.13 * mm});
            skCircle(sketch, "E18.32.0.0", {"center": v(16.5, -18.53) * mm, "radius": 0.13 * mm});
            skCircle(sketch, "E18.33.0.0", {"center": v(17, -18.53) * mm, "radius": 0.13 * mm});
            skCircle(sketch, "E18.34.0.0", {"center": v(17.51, -18.53) * mm, "radius": 0.13 * mm});
            skCircle(sketch, "E18.35.0.0", {"center": v(18.02, -18.53) * mm, "radius": 0.13 * mm});
            skCircle(sketch, "E18.36.0.0", {"center": v(18.53, -18.53) * mm, "radius": 0.13 * mm});
            skCircle(sketch, "E18.37.0.0", {"center": v(19.03, -18.53) * mm, "radius": 0.13 * mm});
            skCircle(sketch, "E18.38.0.0", {"center": v(19.54, -18.53) * mm, "radius": 0.13 * mm});
            skCircle(sketch, "E18.39.0.0", {"center": v(20.05, -18.53) * mm, "radius": 0.13 * mm});
            skCircle(sketch, "E18.40.0.0", {"center": v(20.56, -18.53) * mm, "radius": 0.13 * mm});
            skCircle(sketch, "E18.41.0.0", {"center": v(21.07, -18.53) * mm, "radius": 0.13 * mm});
            skCircle(sketch, "E18.42.0.0", {"center": v(21.57, -18.53) * mm, "radius": 0.13 * mm});
            skCircle(sketch, "E18.43.0.0", {"center": v(22.08, -18.53) * mm, "radius": 0.13 * mm});
            skCircle(sketch, "E18.44.0.0", {"center": v(22.6, -18.53) * mm, "radius": 0.13 * mm});
            skCircle(sketch, "E18.45.0.0", {"center": v(23.1, -18.53) * mm, "radius": 0.13 * mm});
            skCircle(sketch, "E18.46.0.0", {"center": v(23.6, -18.53) * mm, "radius": 0.13 * mm});
            skCircle(sketch, "E18.47.0.0", {"center": v(24.11, -18.53) * mm, "radius": 0.13 * mm});
            skCircle(sketch, "E18.48.0.0", {"center": v(24.62, -18.53) * mm, "radius": 0.13 * mm});
            skCircle(sketch, "E18.49.0.0", {"center": v(25.13, -18.53) * mm, "radius": 0.13 * mm});
            skCircle(sketch, "E18.50.0.0", {"center": v(25.64, -18.53) * mm, "radius": 0.13 * mm});
            skCircle(sketch, "E18.51.0.0", {"center": v(26.15, -18.53) * mm, "radius": 0.13 * mm});
            skCircle(sketch, "E18.52.0.0", {"center": v(26.65, -18.53) * mm, "radius": 0.13 * mm});
            skCircle(sketch, "E18.53.0.0", {"center": v(27.16, -18.53) * mm, "radius": 0.13 * mm});
            skCircle(sketch, "E18.54.0.0", {"center": v(27.67, -18.53) * mm, "radius": 0.13 * mm});
            skCircle(sketch, "E18.55.0.0", {"center": v(28.18, -18.53) * mm, "radius": 0.13 * mm});
            skCircle(sketch, "E18.56.0.0", {"center": v(28.69, -18.53) * mm, "radius": 0.13 * mm});
            skCircle(sketch, "E18.57.0.0", {"center": v(29.2, -18.53) * mm, "radius": 0.13 * mm});
            skCircle(sketch, "E18.58.0.0", {"center": v(29.7, -18.53) * mm, "radius": 0.13 * mm});
            skCircle(sketch, "E18.59.0.0", {"center": v(30.21, -18.53) * mm, "radius": 0.13 * mm});
            skCircle(sketch, "E18.60.0.0", {"center": v(30.72, -18.53) * mm, "radius": 0.13 * mm});
            skCircle(sketch, "E18.61.0.0", {"center": v(31.23, -18.53) * mm, "radius": 0.13 * mm});
            skCircle(sketch, "E18.62.0.0", {"center": v(31.73, -18.53) * mm, "radius": 0.13 * mm});
            skCircle(sketch, "E18.63.0.0", {"center": v(32.24, -18.53) * mm, "radius": 0.13 * mm});
            skCircle(sketch, "E18.64.0.0", {"center": v(32.75, -18.53) * mm, "radius": 0.13 * mm});
            skCircle(sketch, "E18.65.0.0", {"center": v(33.26, -18.53) * mm, "radius": 0.13 * mm});
            skCircle(sketch, "E18.66.0.0", {"center": v(33.77, -18.53) * mm, "radius": 0.13 * mm});
            skCircle(sketch, "E18.67.0.0", {"center": v(34.27, -18.53) * mm, "radius": 0.13 * mm});
            skCircle(sketch, "E18.68.0.0", {"center": v(34.78, -18.53) * mm, "radius": 0.13 * mm});
            skCircle(sketch, "E18.69.0.0", {"center": v(35.3, -18.53) * mm, "radius": 0.13 * mm});
            skCircle(sketch, "E18.70.0.0", {"center": v(35.8, -18.53) * mm, "radius": 0.13 * mm});
            skCircle(sketch, "E18.71.0.0", {"center": v(36.3, -18.53) * mm, "radius": 0.13 * mm});
            skCircle(sketch, "E18.72.0.0", {"center": v(36.81, -18.53) * mm, "radius": 0.13 * mm});
            skCircle(sketch, "E18.73.0.0", {"center": v(37.32, -18.53) * mm, "radius": 0.13 * mm});
            skCircle(sketch, "E18.74.0.0", {"center": v(37.83, -18.53) * mm, "radius": 0.13 * mm});
            skCircle(sketch, "E18.75.0.0", {"center": v(38.34, -18.53) * mm, "radius": 0.13 * mm});
            skCircle(sketch, "E18.76.0.0", {"center": v(38.85, -18.53) * mm, "radius": 0.13 * mm});
            skCircle(sketch, "E18.77.0.0", {"center": v(39.35, -18.53) * mm, "radius": 0.13 * mm});
            skCircle(sketch, "E18.78.0.0", {"center": v(39.86, -18.53) * mm, "radius": 0.13 * mm});
            skCircle(sketch, "E18.79.0.0", {"center": v(40.37, -18.53) * mm, "radius": 0.13 * mm});
            skCircle(sketch, "E18.80.0.0", {"center": v(40.88, -18.53) * mm, "radius": 0.13 * mm});
            skCircle(sketch, "E18.81.0.0", {"center": v(41.39, -18.53) * mm, "radius": 0.13 * mm});
            skCircle(sketch, "E18.82.0.0", {"center": v(41.9, -18.53) * mm, "radius": 0.13 * mm});
            skCircle(sketch, "E18.83.0.0", {"center": v(42.4, -18.53) * mm, "radius": 0.13 * mm});
            skCircle(sketch, "E18.84.0.0", {"center": v(42.91, -18.53) * mm, "radius": 0.13 * mm});
            skCircle(sketch, "E18.85.0.0", {"center": v(43.42, -18.53) * mm, "radius": 0.13 * mm});
            skCircle(sketch, "E18.86.0.0", {"center": v(43.93, -18.53) * mm, "radius": 0.13 * mm});
            skCircle(sketch, "E18.87.0.0", {"center": v(44.43, -18.53) * mm, "radius": 0.13 * mm});
            skCircle(sketch, "E18.88.0.0", {"center": v(44.94, -18.53) * mm, "radius": 0.13 * mm});
            skCircle(sketch, "E18.89.0.0", {"center": v(45.45, -18.53) * mm, "radius": 0.13 * mm});
            skCircle(sketch, "E18.90.0.0", {"center": v(45.96, -18.53) * mm, "radius": 0.13 * mm});
            skCircle(sketch, "E18.91.0.0", {"center": v(46.47, -18.53) * mm, "radius": 0.13 * mm});
            skCircle(sketch, "E18.92.0.0", {"center": v(46.97, -18.53) * mm, "radius": 0.13 * mm});
            skCircle(sketch, "E18.93.0.0", {"center": v(47.48, -18.53) * mm, "radius": 0.13 * mm});
            skCircle(sketch, "E18.94.0.0", {"center": v(48, -18.53) * mm, "radius": 0.13 * mm});
            skLineSegment(sketch, "E18.direction1", {"start": v(0.24, -18.53) * mm, "end": v(0.75, -18.53) * mm, "construction": true});
            skCircle(sketch, "E19.1.0.0", {"center": v(0.74, -18.02) * mm, "radius": 0.13 * mm});
            skCircle(sketch, "E19.2.0.0", {"center": v(1.25, -18.02) * mm, "radius": 0.13 * mm});
            skCircle(sketch, "E19.3.0.0", {"center": v(1.76, -18.02) * mm, "radius": 0.13 * mm});
            skCircle(sketch, "E19.4.0.0", {"center": v(2.27, -18.02) * mm, "radius": 0.13 * mm});
            skCircle(sketch, "E19.5.0.0", {"center": v(2.77, -18.02) * mm, "radius": 0.13 * mm});
            skCircle(sketch, "E19.6.0.0", {"center": v(3.28, -18.02) * mm, "radius": 0.13 * mm});
            skCircle(sketch, "E19.7.0.0", {"center": v(3.79, -18.02) * mm, "radius": 0.13 * mm});
            skCircle(sketch, "E19.8.0.0", {"center": v(4.3, -18.02) * mm, "radius": 0.13 * mm});
            skCircle(sketch, "E19.9.0.0", {"center": v(4.8, -18.02) * mm, "radius": 0.13 * mm});
            skCircle(sketch, "E19.10.0.0", {"center": v(5.31, -18.02) * mm, "radius": 0.13 * mm});
            skCircle(sketch, "E19.11.0.0", {"center": v(5.82, -18.02) * mm, "radius": 0.13 * mm});
            skCircle(sketch, "E19.12.0.0", {"center": v(6.33, -18.02) * mm, "radius": 0.13 * mm});
            skCircle(sketch, "E19.13.0.0", {"center": v(6.84, -18.02) * mm, "radius": 0.13 * mm});
            skCircle(sketch, "E19.14.0.0", {"center": v(7.35, -18.02) * mm, "radius": 0.13 * mm});
            skCircle(sketch, "E19.15.0.0", {"center": v(7.85, -18.02) * mm, "radius": 0.13 * mm});
            skCircle(sketch, "E19.16.0.0", {"center": v(8.36, -18.02) * mm, "radius": 0.13 * mm});
            skCircle(sketch, "E19.17.0.0", {"center": v(8.87, -18.02) * mm, "radius": 0.13 * mm});
            skCircle(sketch, "E19.18.0.0", {"center": v(9.38, -18.02) * mm, "radius": 0.13 * mm});
            skCircle(sketch, "E19.19.0.0", {"center": v(9.89, -18.02) * mm, "radius": 0.13 * mm});
            skCircle(sketch, "E19.20.0.0", {"center": v(10.4, -18.02) * mm, "radius": 0.13 * mm});
            skCircle(sketch, "E19.21.0.0", {"center": v(10.9, -18.02) * mm, "radius": 0.13 * mm});
            skCircle(sketch, "E19.22.0.0", {"center": v(11.4, -18.02) * mm, "radius": 0.13 * mm});
            skCircle(sketch, "E19.23.0.0", {"center": v(11.92, -18.02) * mm, "radius": 0.13 * mm});
            skCircle(sketch, "E19.24.0.0", {"center": v(12.43, -18.02) * mm, "radius": 0.13 * mm});
            skCircle(sketch, "E19.25.0.0", {"center": v(12.93, -18.02) * mm, "radius": 0.13 * mm});
            skCircle(sketch, "E19.26.0.0", {"center": v(13.44, -18.02) * mm, "radius": 0.13 * mm});
            skCircle(sketch, "E19.27.0.0", {"center": v(13.95, -18.02) * mm, "radius": 0.13 * mm});
            skCircle(sketch, "E19.28.0.0", {"center": v(14.46, -18.02) * mm, "radius": 0.13 * mm});
            skCircle(sketch, "E19.29.0.0", {"center": v(14.97, -18.02) * mm, "radius": 0.13 * mm});
            skCircle(sketch, "E19.30.0.0", {"center": v(15.47, -18.02) * mm, "radius": 0.13 * mm});
            skCircle(sketch, "E19.31.0.0", {"center": v(15.98, -18.02) * mm, "radius": 0.13 * mm});
            skCircle(sketch, "E19.32.0.0", {"center": v(16.49, -18.02) * mm, "radius": 0.13 * mm});
            skCircle(sketch, "E19.33.0.0", {"center": v(17, -18.02) * mm, "radius": 0.13 * mm});
            skCircle(sketch, "E19.34.0.0", {"center": v(17.5, -18.02) * mm, "radius": 0.13 * mm});
            skCircle(sketch, "E19.35.0.0", {"center": v(18.01, -18.02) * mm, "radius": 0.13 * mm});
            skCircle(sketch, "E19.36.0.0", {"center": v(18.52, -18.02) * mm, "radius": 0.13 * mm});
            skCircle(sketch, "E19.37.0.0", {"center": v(19.03, -18.02) * mm, "radius": 0.13 * mm});
            skCircle(sketch, "E19.38.0.0", {"center": v(19.54, -18.02) * mm, "radius": 0.13 * mm});
            skCircle(sketch, "E19.39.0.0", {"center": v(20.05, -18.02) * mm, "radius": 0.13 * mm});
            skCircle(sketch, "E19.40.0.0", {"center": v(20.55, -18.02) * mm, "radius": 0.13 * mm});
            skCircle(sketch, "E19.41.0.0", {"center": v(21.06, -18.02) * mm, "radius": 0.13 * mm});
            skCircle(sketch, "E19.42.0.0", {"center": v(21.57, -18.02) * mm, "radius": 0.13 * mm});
            skCircle(sketch, "E19.43.0.0", {"center": v(22.08, -18.02) * mm, "radius": 0.13 * mm});
            skCircle(sketch, "E19.44.0.0", {"center": v(22.59, -18.02) * mm, "radius": 0.13 * mm});
            skCircle(sketch, "E19.45.0.0", {"center": v(23.1, -18.02) * mm, "radius": 0.13 * mm});
            skCircle(sketch, "E19.46.0.0", {"center": v(23.6, -18.02) * mm, "radius": 0.13 * mm});
            skCircle(sketch, "E19.47.0.0", {"center": v(24.1, -18.02) * mm, "radius": 0.13 * mm});
            skCircle(sketch, "E19.48.0.0", {"center": v(24.62, -18.02) * mm, "radius": 0.13 * mm});
            skCircle(sketch, "E19.49.0.0", {"center": v(25.13, -18.02) * mm, "radius": 0.13 * mm});
            skCircle(sketch, "E19.50.0.0", {"center": v(25.63, -18.02) * mm, "radius": 0.13 * mm});
            skCircle(sketch, "E19.51.0.0", {"center": v(26.14, -18.02) * mm, "radius": 0.13 * mm});
            skCircle(sketch, "E19.52.0.0", {"center": v(26.65, -18.02) * mm, "radius": 0.13 * mm});
            skCircle(sketch, "E19.53.0.0", {"center": v(27.16, -18.02) * mm, "radius": 0.13 * mm});
            skCircle(sketch, "E19.54.0.0", {"center": v(27.67, -18.02) * mm, "radius": 0.13 * mm});
            skCircle(sketch, "E19.55.0.0", {"center": v(28.17, -18.02) * mm, "radius": 0.13 * mm});
            skCircle(sketch, "E19.56.0.0", {"center": v(28.68, -18.02) * mm, "radius": 0.13 * mm});
            skCircle(sketch, "E19.57.0.0", {"center": v(29.19, -18.02) * mm, "radius": 0.13 * mm});
            skCircle(sketch, "E19.58.0.0", {"center": v(29.7, -18.02) * mm, "radius": 0.13 * mm});
            skCircle(sketch, "E19.59.0.0", {"center": v(30.2, -18.02) * mm, "radius": 0.13 * mm});
            skCircle(sketch, "E19.60.0.0", {"center": v(30.71, -18.02) * mm, "radius": 0.13 * mm});
            skCircle(sketch, "E19.61.0.0", {"center": v(31.22, -18.02) * mm, "radius": 0.13 * mm});
            skCircle(sketch, "E19.62.0.0", {"center": v(31.73, -18.02) * mm, "radius": 0.13 * mm});
            skCircle(sketch, "E19.63.0.0", {"center": v(32.24, -18.02) * mm, "radius": 0.13 * mm});
            skCircle(sketch, "E19.64.0.0", {"center": v(32.75, -18.02) * mm, "radius": 0.13 * mm});
            skCircle(sketch, "E19.65.0.0", {"center": v(33.25, -18.02) * mm, "radius": 0.13 * mm});
            skCircle(sketch, "E19.66.0.0", {"center": v(33.76, -18.02) * mm, "radius": 0.13 * mm});
            skCircle(sketch, "E19.67.0.0", {"center": v(34.27, -18.02) * mm, "radius": 0.13 * mm});
            skCircle(sketch, "E19.68.0.0", {"center": v(34.78, -18.02) * mm, "radius": 0.13 * mm});
            skCircle(sketch, "E19.69.0.0", {"center": v(35.29, -18.02) * mm, "radius": 0.13 * mm});
            skCircle(sketch, "E19.70.0.0", {"center": v(35.8, -18.02) * mm, "radius": 0.13 * mm});
            skCircle(sketch, "E19.71.0.0", {"center": v(36.3, -18.02) * mm, "radius": 0.13 * mm});
            skCircle(sketch, "E19.72.0.0", {"center": v(36.8, -18.02) * mm, "radius": 0.13 * mm});
            skCircle(sketch, "E19.73.0.0", {"center": v(37.32, -18.02) * mm, "radius": 0.13 * mm});
            skCircle(sketch, "E19.74.0.0", {"center": v(37.83, -18.02) * mm, "radius": 0.13 * mm});
            skCircle(sketch, "E19.75.0.0", {"center": v(38.33, -18.02) * mm, "radius": 0.13 * mm});
            skCircle(sketch, "E19.76.0.0", {"center": v(38.84, -18.02) * mm, "radius": 0.13 * mm});
            skCircle(sketch, "E19.77.0.0", {"center": v(39.35, -18.02) * mm, "radius": 0.13 * mm});
            skCircle(sketch, "E19.78.0.0", {"center": v(39.86, -18.02) * mm, "radius": 0.13 * mm});
            skCircle(sketch, "E19.79.0.0", {"center": v(40.37, -18.02) * mm, "radius": 0.13 * mm});
            skCircle(sketch, "E19.80.0.0", {"center": v(40.87, -18.02) * mm, "radius": 0.13 * mm});
            skCircle(sketch, "E19.81.0.0", {"center": v(41.38, -18.02) * mm, "radius": 0.13 * mm});
            skCircle(sketch, "E19.82.0.0", {"center": v(41.89, -18.02) * mm, "radius": 0.13 * mm});
            skCircle(sketch, "E19.83.0.0", {"center": v(42.4, -18.02) * mm, "radius": 0.13 * mm});
            skCircle(sketch, "E19.84.0.0", {"center": v(42.9, -18.02) * mm, "radius": 0.13 * mm});
            skCircle(sketch, "E19.85.0.0", {"center": v(43.41, -18.02) * mm, "radius": 0.13 * mm});
            skCircle(sketch, "E19.86.0.0", {"center": v(43.92, -18.02) * mm, "radius": 0.13 * mm});
            skCircle(sketch, "E19.87.0.0", {"center": v(44.43, -18.02) * mm, "radius": 0.13 * mm});
            skCircle(sketch, "E19.88.0.0", {"center": v(44.94, -18.02) * mm, "radius": 0.13 * mm});
            skCircle(sketch, "E19.89.0.0", {"center": v(45.45, -18.02) * mm, "radius": 0.13 * mm});
            skCircle(sketch, "E19.90.0.0", {"center": v(45.95, -18.02) * mm, "radius": 0.13 * mm});
            skCircle(sketch, "E19.91.0.0", {"center": v(46.46, -18.02) * mm, "radius": 0.13 * mm});
            skCircle(sketch, "E19.92.0.0", {"center": v(46.97, -18.02) * mm, "radius": 0.13 * mm});
            skCircle(sketch, "E19.93.0.0", {"center": v(47.48, -18.02) * mm, "radius": 0.13 * mm});
            skCircle(sketch, "E19.94.0.0", {"center": v(47.99, -18.02) * mm, "radius": 0.13 * mm});
            skLineSegment(sketch, "E19.direction1", {"start": v(0.23, -18.02) * mm, "end": v(0.74, -18.02) * mm, "construction": true});
            skCircle(sketch, "E20.1.0.0", {"center": v(0.74, -17.51) * mm, "radius": 0.13 * mm});
            skCircle(sketch, "E20.2.0.0", {"center": v(1.24, -17.51) * mm, "radius": 0.13 * mm});
            skCircle(sketch, "E20.3.0.0", {"center": v(1.75, -17.51) * mm, "radius": 0.13 * mm});
            skCircle(sketch, "E20.4.0.0", {"center": v(2.26, -17.51) * mm, "radius": 0.13 * mm});
            skCircle(sketch, "E20.5.0.0", {"center": v(2.77, -17.51) * mm, "radius": 0.13 * mm});
            skCircle(sketch, "E20.6.0.0", {"center": v(3.28, -17.51) * mm, "radius": 0.13 * mm});
            skCircle(sketch, "E20.7.0.0", {"center": v(3.78, -17.51) * mm, "radius": 0.13 * mm});
            skCircle(sketch, "E20.8.0.0", {"center": v(4.3, -17.51) * mm, "radius": 0.13 * mm});
            skCircle(sketch, "E20.9.0.0", {"center": v(4.8, -17.51) * mm, "radius": 0.13 * mm});
            skCircle(sketch, "E20.10.0.0", {"center": v(5.3, -17.51) * mm, "radius": 0.13 * mm});
            skCircle(sketch, "E20.11.0.0", {"center": v(5.82, -17.51) * mm, "radius": 0.13 * mm});
            skCircle(sketch, "E20.12.0.0", {"center": v(6.32, -17.51) * mm, "radius": 0.13 * mm});
            skCircle(sketch, "E20.13.0.0", {"center": v(6.83, -17.51) * mm, "radius": 0.13 * mm});
            skCircle(sketch, "E20.14.0.0", {"center": v(7.34, -17.51) * mm, "radius": 0.13 * mm});
            skCircle(sketch, "E20.15.0.0", {"center": v(7.85, -17.51) * mm, "radius": 0.13 * mm});
            skCircle(sketch, "E20.16.0.0", {"center": v(8.36, -17.51) * mm, "radius": 0.13 * mm});
            skCircle(sketch, "E20.17.0.0", {"center": v(8.86, -17.51) * mm, "radius": 0.13 * mm});
            skCircle(sketch, "E20.18.0.0", {"center": v(9.37, -17.51) * mm, "radius": 0.13 * mm});
            skCircle(sketch, "E20.19.0.0", {"center": v(9.88, -17.51) * mm, "radius": 0.13 * mm});
            skCircle(sketch, "E20.20.0.0", {"center": v(10.39, -17.51) * mm, "radius": 0.13 * mm});
            skCircle(sketch, "E20.21.0.0", {"center": v(10.9, -17.51) * mm, "radius": 0.13 * mm});
            skCircle(sketch, "E20.22.0.0", {"center": v(11.4, -17.51) * mm, "radius": 0.13 * mm});
            skCircle(sketch, "E20.23.0.0", {"center": v(11.91, -17.51) * mm, "radius": 0.13 * mm});
            skCircle(sketch, "E20.24.0.0", {"center": v(12.42, -17.51) * mm, "radius": 0.13 * mm});
            skCircle(sketch, "E20.25.0.0", {"center": v(12.93, -17.51) * mm, "radius": 0.13 * mm});
            skCircle(sketch, "E20.26.0.0", {"center": v(13.44, -17.51) * mm, "radius": 0.13 * mm});
            skCircle(sketch, "E20.27.0.0", {"center": v(13.94, -17.51) * mm, "radius": 0.13 * mm});
            skCircle(sketch, "E20.28.0.0", {"center": v(14.45, -17.51) * mm, "radius": 0.13 * mm});
            skCircle(sketch, "E20.29.0.0", {"center": v(14.96, -17.51) * mm, "radius": 0.13 * mm});
            skCircle(sketch, "E20.30.0.0", {"center": v(15.47, -17.51) * mm, "radius": 0.13 * mm});
            skCircle(sketch, "E20.31.0.0", {"center": v(15.98, -17.51) * mm, "radius": 0.13 * mm});
            skCircle(sketch, "E20.32.0.0", {"center": v(16.48, -17.51) * mm, "radius": 0.13 * mm});
            skCircle(sketch, "E20.33.0.0", {"center": v(17, -17.51) * mm, "radius": 0.13 * mm});
            skCircle(sketch, "E20.34.0.0", {"center": v(17.5, -17.51) * mm, "radius": 0.13 * mm});
            skCircle(sketch, "E20.35.0.0", {"center": v(18, -17.51) * mm, "radius": 0.13 * mm});
            skCircle(sketch, "E20.36.0.0", {"center": v(18.52, -17.51) * mm, "radius": 0.13 * mm});
            skCircle(sketch, "E20.37.0.0", {"center": v(19.02, -17.51) * mm, "radius": 0.13 * mm});
            skCircle(sketch, "E20.38.0.0", {"center": v(19.53, -17.51) * mm, "radius": 0.13 * mm});
            skCircle(sketch, "E20.39.0.0", {"center": v(20.04, -17.51) * mm, "radius": 0.13 * mm});
            skCircle(sketch, "E20.40.0.0", {"center": v(20.55, -17.51) * mm, "radius": 0.13 * mm});
            skCircle(sketch, "E20.41.0.0", {"center": v(21.06, -17.51) * mm, "radius": 0.13 * mm});
            skCircle(sketch, "E20.42.0.0", {"center": v(21.56, -17.51) * mm, "radius": 0.13 * mm});
            skCircle(sketch, "E20.43.0.0", {"center": v(22.07, -17.51) * mm, "radius": 0.13 * mm});
            skCircle(sketch, "E20.44.0.0", {"center": v(22.58, -17.51) * mm, "radius": 0.13 * mm});
            skCircle(sketch, "E20.45.0.0", {"center": v(23.09, -17.51) * mm, "radius": 0.13 * mm});
            skCircle(sketch, "E20.46.0.0", {"center": v(23.6, -17.51) * mm, "radius": 0.13 * mm});
            skCircle(sketch, "E20.47.0.0", {"center": v(24.1, -17.51) * mm, "radius": 0.13 * mm});
            skCircle(sketch, "E20.48.0.0", {"center": v(24.61, -17.51) * mm, "radius": 0.13 * mm});
            skCircle(sketch, "E20.49.0.0", {"center": v(25.12, -17.51) * mm, "radius": 0.13 * mm});
            skCircle(sketch, "E20.50.0.0", {"center": v(25.63, -17.51) * mm, "radius": 0.13 * mm});
            skCircle(sketch, "E20.51.0.0", {"center": v(26.14, -17.51) * mm, "radius": 0.13 * mm});
            skCircle(sketch, "E20.52.0.0", {"center": v(26.64, -17.51) * mm, "radius": 0.13 * mm});
            skCircle(sketch, "E20.53.0.0", {"center": v(27.15, -17.51) * mm, "radius": 0.13 * mm});
            skCircle(sketch, "E20.54.0.0", {"center": v(27.66, -17.51) * mm, "radius": 0.13 * mm});
            skCircle(sketch, "E20.55.0.0", {"center": v(28.17, -17.51) * mm, "radius": 0.13 * mm});
            skCircle(sketch, "E20.56.0.0", {"center": v(28.68, -17.51) * mm, "radius": 0.13 * mm});
            skCircle(sketch, "E20.57.0.0", {"center": v(29.18, -17.51) * mm, "radius": 0.13 * mm});
            skCircle(sketch, "E20.58.0.0", {"center": v(29.7, -17.51) * mm, "radius": 0.13 * mm});
            skCircle(sketch, "E20.59.0.0", {"center": v(30.2, -17.51) * mm, "radius": 0.13 * mm});
            skCircle(sketch, "E20.60.0.0", {"center": v(30.7, -17.51) * mm, "radius": 0.13 * mm});
            skCircle(sketch, "E20.61.0.0", {"center": v(31.22, -17.51) * mm, "radius": 0.13 * mm});
            skCircle(sketch, "E20.62.0.0", {"center": v(31.72, -17.51) * mm, "radius": 0.13 * mm});
            skCircle(sketch, "E20.63.0.0", {"center": v(32.23, -17.51) * mm, "radius": 0.13 * mm});
            skCircle(sketch, "E20.64.0.0", {"center": v(32.74, -17.51) * mm, "radius": 0.13 * mm});
            skCircle(sketch, "E20.65.0.0", {"center": v(33.25, -17.51) * mm, "radius": 0.13 * mm});
            skCircle(sketch, "E20.66.0.0", {"center": v(33.76, -17.51) * mm, "radius": 0.13 * mm});
            skCircle(sketch, "E20.67.0.0", {"center": v(34.26, -17.51) * mm, "radius": 0.13 * mm});
            skCircle(sketch, "E20.68.0.0", {"center": v(34.77, -17.51) * mm, "radius": 0.13 * mm});
            skCircle(sketch, "E20.69.0.0", {"center": v(35.28, -17.51) * mm, "radius": 0.13 * mm});
            skCircle(sketch, "E20.70.0.0", {"center": v(35.79, -17.51) * mm, "radius": 0.13 * mm});
            skCircle(sketch, "E20.71.0.0", {"center": v(36.3, -17.51) * mm, "radius": 0.13 * mm});
            skCircle(sketch, "E20.72.0.0", {"center": v(36.8, -17.51) * mm, "radius": 0.13 * mm});
            skCircle(sketch, "E20.73.0.0", {"center": v(37.31, -17.51) * mm, "radius": 0.13 * mm});
            skCircle(sketch, "E20.74.0.0", {"center": v(37.82, -17.51) * mm, "radius": 0.13 * mm});
            skCircle(sketch, "E20.75.0.0", {"center": v(38.33, -17.51) * mm, "radius": 0.13 * mm});
            skCircle(sketch, "E20.76.0.0", {"center": v(38.84, -17.51) * mm, "radius": 0.13 * mm});
            skCircle(sketch, "E20.77.0.0", {"center": v(39.34, -17.51) * mm, "radius": 0.13 * mm});
            skCircle(sketch, "E20.78.0.0", {"center": v(39.85, -17.51) * mm, "radius": 0.13 * mm});
            skCircle(sketch, "E20.79.0.0", {"center": v(40.36, -17.51) * mm, "radius": 0.13 * mm});
            skCircle(sketch, "E20.80.0.0", {"center": v(40.87, -17.51) * mm, "radius": 0.13 * mm});
            skCircle(sketch, "E20.81.0.0", {"center": v(41.38, -17.51) * mm, "radius": 0.13 * mm});
            skCircle(sketch, "E20.82.0.0", {"center": v(41.88, -17.51) * mm, "radius": 0.13 * mm});
            skCircle(sketch, "E20.83.0.0", {"center": v(42.4, -17.51) * mm, "radius": 0.13 * mm});
            skCircle(sketch, "E20.84.0.0", {"center": v(42.9, -17.51) * mm, "radius": 0.13 * mm});
            skCircle(sketch, "E20.85.0.0", {"center": v(43.4, -17.51) * mm, "radius": 0.13 * mm});
            skCircle(sketch, "E20.86.0.0", {"center": v(43.92, -17.51) * mm, "radius": 0.13 * mm});
            skCircle(sketch, "E20.87.0.0", {"center": v(44.42, -17.51) * mm, "radius": 0.13 * mm});
            skCircle(sketch, "E20.88.0.0", {"center": v(44.93, -17.51) * mm, "radius": 0.13 * mm});
            skCircle(sketch, "E20.89.0.0", {"center": v(45.44, -17.51) * mm, "radius": 0.13 * mm});
            skCircle(sketch, "E20.90.0.0", {"center": v(45.95, -17.51) * mm, "radius": 0.13 * mm});
            skCircle(sketch, "E20.91.0.0", {"center": v(46.46, -17.51) * mm, "radius": 0.13 * mm});
            skCircle(sketch, "E20.92.0.0", {"center": v(46.96, -17.51) * mm, "radius": 0.13 * mm});
            skCircle(sketch, "E20.93.0.0", {"center": v(47.47, -17.51) * mm, "radius": 0.13 * mm});
            skCircle(sketch, "E20.94.0.0", {"center": v(47.98, -17.51) * mm, "radius": 0.13 * mm});
            skLineSegment(sketch, "E20.direction1", {"start": v(0.23, -17.51) * mm, "end": v(0.74, -17.51) * mm, "construction": true});
            skSolve(sketch);
        }
        {
            var Q0;
            {var subQ3=sQuery(id+"F2.wireOp",EDGE,"E7.bottom");Q0=makeQuery(id+"F2.imprint","IMPRINT",FACE,{"disambiguationData":[TD([[makeQuery(id+"F2.imprint","IMPRINT",EDGE,{"derivedFrom":subQ3}),1.0]])]});}
            extrude(context, id + "F3", {"entities" : qUnion([Q0]), "operationType" : NewBodyOperationType.ADD, "oppositeDirection" : true, "depth" : 3.17 * mm});
        }
    });
